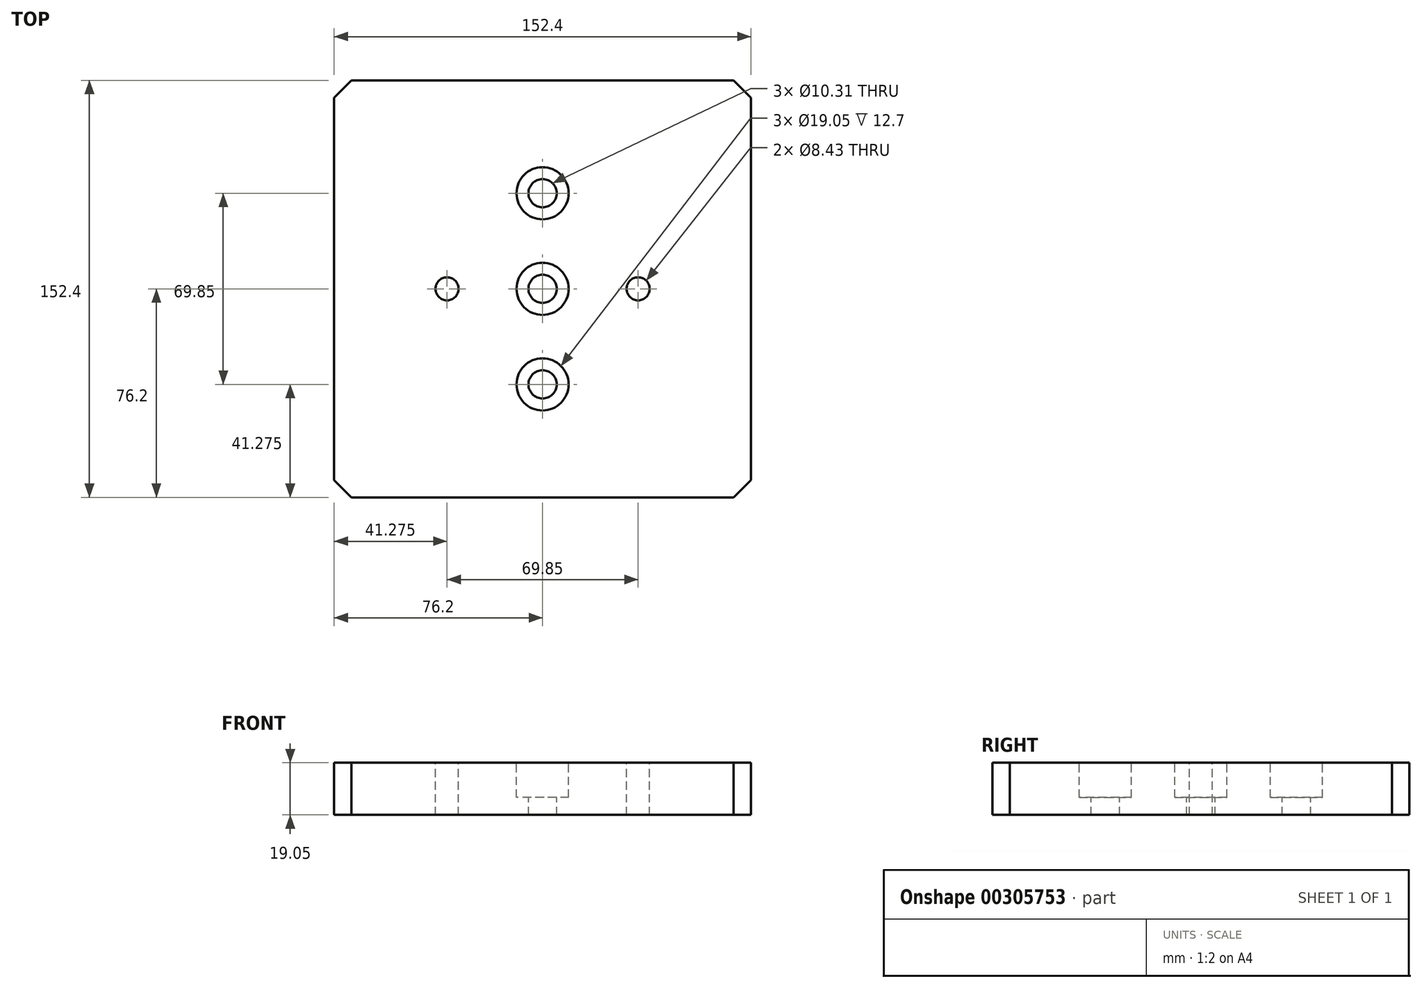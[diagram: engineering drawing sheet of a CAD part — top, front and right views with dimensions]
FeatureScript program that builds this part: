
annotation { "Feature Type Name" : "Feature", "Feature Type Description" : "" }
export const myFeature = defineFeature(function(context is Context, id is Id, definition is map)
    precondition{}
    {
        {
            var Q0;
            Q0=qCreatedBy(makeId("Top.planeOp"),FACE);
            var sketch = newSketch(context, id + "F0", { "sketchPlane" : qUnion([Q0])});
            skLineSegment(sketch, "E0.bottom", {"start": v(-76.2, 76.2) * mm, "end": v(76.2, 76.2) * mm});
            skLineSegment(sketch, "E0.top", {"start": v(-76.2, -76.2) * mm, "end": v(76.2, -76.2) * mm});
            skLineSegment(sketch, "E0.left", {"start": v(-76.2, 76.2) * mm, "end": v(-76.2, -76.2) * mm});
            skLineSegment(sketch, "E0.right", {"start": v(76.2, 76.2) * mm, "end": v(76.2, -76.2) * mm});
            skPoint(sketch, "E0.middle", {"position": v(0, 0) * mm});
            skSolve(sketch);
        }
        {
            var Q0;
            Q0 = qSketchRegion(id + "F0", true);
            extrude(context, id + "F1", {"entities" : qUnion([Q0]), "depth" : 19.05 * mm});
        }
        {
            var Q0;
            Q0=makeQuery(id+"F1.opExtrude","CAP_FACE",FACE,{"disambiguationData":[OSD([sQuery(id+"F0.wireOp",EDGE,"E0.bottom"),sQuery(id+"F0.wireOp",EDGE,"E0.top"),sQuery(id+"F0.wireOp",EDGE,"E0.left"),sQuery(id+"F0.wireOp",EDGE,"E0.right")])],"isStart":false});
            var sketch = newSketch(context, id + "F2", { "sketchPlane" : qUnion([Q0])});
            skLineSegment(sketch, "E1", {"start": v(0, 101.34) * mm, "end": v(0, -100.66) * mm, "construction": true});
            skLineSegment(sketch, "E2", {"start": v(-108.19, 0) * mm, "end": v(94.84, 0) * mm, "construction": true});
            skPoint(sketch, "E2.endSnap0", {"position": v(76.2, 0) * mm});
            skLineSegment(sketch, "E3.0", {"start": v(-34.93, 101.34) * mm, "end": v(-34.92, -100.66) * mm, "construction": true});
            skLineSegment(sketch, "E4.0", {"start": v(-108.19, -34.93) * mm, "end": v(94.84, -34.92) * mm, "construction": true});
            skPoint(sketch, "E5", {"position": v(-34.92, 0) * mm});
            skPoint(sketch, "E6", {"position": v(0, 0) * mm});
            skPoint(sketch, "E7", {"position": v(0, -34.93) * mm});
            skPoint(sketch, "E8.MirrorP", {"position": v(0, 34.93) * mm});
            skPoint(sketch, "E9.MirrorP", {"position": v(34.92, 0) * mm});
            skSolve(sketch);
        }
        {
            var Q0;
            Q0=sQuery(id+"F2.wireOp",VERTEX,"E5");
            var Q1;
            Q1=sQuery(id+"F2.wireOp",VERTEX,"E9.MirrorP");
            var Q2;
            Q2=makeQuery(id+"F1.opExtrude","SWEPT_BODY",BODY,{"disambiguationData":[OSD([sQuery(id+"F0.wireOp",EDGE,"E0.bottom"),sQuery(id+"F0.wireOp",EDGE,"E0.top"),sQuery(id+"F0.wireOp",EDGE,"E0.left"),sQuery(id+"F0.wireOp",EDGE,"E0.right")])]});
            hole(context, id + "F3", {"style" : HoleStyle.SIMPLE, "endStyle" : HoleEndStyle.THROUGH, "standardTappedOrClearance" : lookupTablePath({ "standard" : "ANSI", "engagement" : "75%", "pitch" : "24 tpi", "size" : "3/8", "type" : "Tapped" }), "standardBlindInLast" : lookupTablePath({ "standard" : "ANSI", "engagement" : "75%", "pitch" : "24 tpi", "size" : "3/8", "type" : "Tapped" }), "holeDiameter" : 8.43 * mm, "showTappedDepth" : true, "tappedDepth" : 24.13 * mm, "tapClearance" : 3, "startFromSketch" : true, "locations" : qUnion([Q0, Q1]), "scope" : qUnion([Q2]), "majorDiameter" : 9.53 * mm});
        }
        {
            var Q0;
            Q0=sQuery(id+"F2.wireOp",VERTEX,"E8.MirrorP");
            var Q1;
            Q1=sQuery(id+"F2.wireOp",VERTEX,"E6");
            var Q2;
            Q2=sQuery(id+"F2.wireOp",VERTEX,"E7");
            var Q3;
            Q3=makeQuery(id+"F1.opExtrude","SWEPT_BODY",BODY,{"disambiguationData":[OSD([sQuery(id+"F0.wireOp",EDGE,"E0.bottom"),sQuery(id+"F0.wireOp",EDGE,"E0.top"),sQuery(id+"F0.wireOp",EDGE,"E0.left"),sQuery(id+"F0.wireOp",EDGE,"E0.right")])]});
            hole(context, id + "F4", {"style" : HoleStyle.C_BORE, "endStyle" : HoleEndStyle.THROUGH, "holeDiameter" : 10.3 * mm, "cBoreDiameter" : 19.05 * mm, "cBoreDepth" : 12.7 * mm, "tappedDepth" : 24.13 * mm, "tapClearance" : 3, "startFromSketch" : true, "locations" : qUnion([Q0, Q1, Q2]), "scope" : qUnion([Q3])});
        }
        {
            var Q0;
            Q0=makeQuery(id+"F1.opExtrude","SWEPT_EDGE",EDGE,{"disambiguationData":[OSD([sQuery(id+"F0.wireOp",EDGE,"E0.bottom"),sQuery(id+"F0.wireOp",EDGE,"E0.left")])]});
            var Q1;
            Q1=makeQuery(id+"F1.opExtrude","SWEPT_EDGE",EDGE,{"disambiguationData":[OSD([sQuery(id+"F0.wireOp",EDGE,"E0.top"),sQuery(id+"F0.wireOp",EDGE,"E0.left")])]});
            var Q2;
            Q2=makeQuery(id+"F1.opExtrude","SWEPT_EDGE",EDGE,{"disambiguationData":[OSD([sQuery(id+"F0.wireOp",EDGE,"E0.top"),sQuery(id+"F0.wireOp",EDGE,"E0.right")])]});
            var Q3;
            Q3=makeQuery(id+"F1.opExtrude","SWEPT_EDGE",EDGE,{"disambiguationData":[OSD([sQuery(id+"F0.wireOp",EDGE,"E0.bottom"),sQuery(id+"F0.wireOp",EDGE,"E0.right")])]});
            chamfer(context, id + "F5", {"entities" : qUnion([Q0, Q1, Q2, Q3]), "width" : 6.35 * mm, "tangentPropagation" : true});
        }
    });
